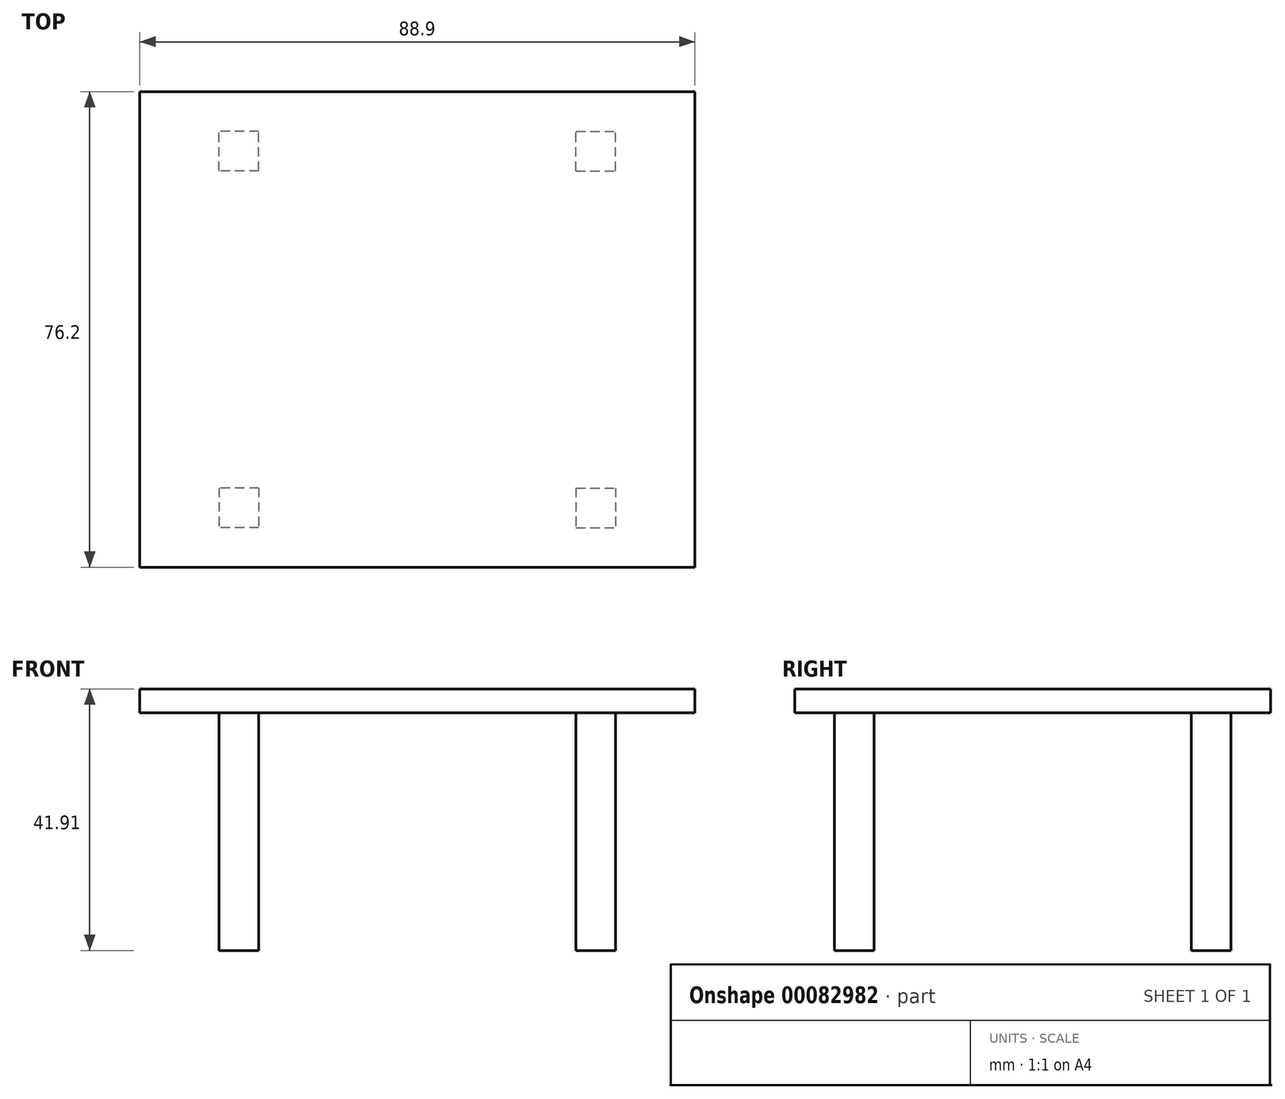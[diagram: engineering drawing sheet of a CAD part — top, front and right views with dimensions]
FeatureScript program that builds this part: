
annotation { "Feature Type Name" : "Feature", "Feature Type Description" : "" }
export const myFeature = defineFeature(function(context is Context, id is Id, definition is map)
    precondition{}
    {
        {
            var Q0;
            Q0=qCreatedBy(makeId("Top.planeOp"),FACE);
            var sketch = newSketch(context, id + "F0", { "sketchPlane" : qUnion([Q0])});
            skLineSegment(sketch, "E0.bottom", {"start": v(-25.4, 25.4) * mm, "end": v(-31.75, 25.4) * mm});
            skLineSegment(sketch, "E0.top", {"start": v(-25.4, 31.75) * mm, "end": v(-31.75, 31.75) * mm});
            skLineSegment(sketch, "E0.left", {"start": v(-25.4, 25.4) * mm, "end": v(-25.4, 31.75) * mm});
            skLineSegment(sketch, "E0.right", {"start": v(-31.75, 25.4) * mm, "end": v(-31.75, 31.75) * mm});
            skSolve(sketch);
        }
        {
            var Q0;
            Q0=makeQuery(id+"F0.imprint","IMPRINT",FACE,{"disambiguationData":[TD([[makeQuery(id+"F0.imprint","IMPRINT",EDGE,{"derivedFrom":sQuery(id+"F0.wireOp",EDGE,"E0.bottom")}),-1.0]])]});
            extrude(context, id + "F1", {"entities" : qUnion([Q0]), "endBound" : BoundingType.SYMMETRIC, "depth" : 38.1 * mm});
        }
        {
            var Q0;
            Q0=makeQuery(id+"F1.opExtrude","SWEPT_BODY",BODY,{"disambiguationData":[OSD([sQuery(id+"F0.wireOp",EDGE,"E0.bottom"),sQuery(id+"F0.wireOp",EDGE,"E0.top"),sQuery(id+"F0.wireOp",EDGE,"E0.left"),sQuery(id+"F0.wireOp",EDGE,"E0.right")])]});
            var Q1;
            Q1=qCreatedBy(makeId("Right.planeOp"),FACE);
            mirror(context, id + "F2", {"entities" : qUnion([Q0]), "mirrorPlane" : qUnion([Q1])});
        }
        {
            var Q0;
            Q0=makeQuery(id+"F1.opExtrude","SWEPT_BODY",BODY,{"disambiguationData":[OSD([sQuery(id+"F0.wireOp",EDGE,"E0.bottom"),sQuery(id+"F0.wireOp",EDGE,"E0.top"),sQuery(id+"F0.wireOp",EDGE,"E0.left"),sQuery(id+"F0.wireOp",EDGE,"E0.right")])]});
            var Q1;
            Q1=makeQuery(id+"F2.opPattern","COPY",BODY,{"derivedFrom":makeQuery(id+"F1.opExtrude","SWEPT_BODY",BODY,{"disambiguationData":[OSD([sQuery(id+"F0.wireOp",EDGE,"E0.bottom"),sQuery(id+"F0.wireOp",EDGE,"E0.top"),sQuery(id+"F0.wireOp",EDGE,"E0.left"),sQuery(id+"F0.wireOp",EDGE,"E0.right")])]}),"instanceName":"1"});
            var Q2;
            Q2=qCreatedBy(makeId("Front.planeOp"),FACE);
            mirror(context, id + "F3", {"entities" : qUnion([Q0, Q1]), "mirrorPlane" : qUnion([Q2])});
        }
        {
            var Q0;
            Q0=makeQuery(id+"F1.opExtrude","CAP_FACE",FACE,{"disambiguationData":[OSD([sQuery(id+"F0.wireOp",EDGE,"E0.bottom"),sQuery(id+"F0.wireOp",EDGE,"E0.top"),sQuery(id+"F0.wireOp",EDGE,"E0.left"),sQuery(id+"F0.wireOp",EDGE,"E0.right")])],"isStart":false});
            var sketch = newSketch(context, id + "F4", { "sketchPlane" : qUnion([Q0])});
            skLineSegment(sketch, "E1.bottom", {"start": v(-44.45, 38.1) * mm, "end": v(44.45, 38.1) * mm});
            skLineSegment(sketch, "E1.top", {"start": v(-44.45, -38.1) * mm, "end": v(44.45, -38.1) * mm});
            skLineSegment(sketch, "E1.left", {"start": v(-44.45, 38.1) * mm, "end": v(-44.45, -38.1) * mm});
            skLineSegment(sketch, "E1.right", {"start": v(44.45, 38.1) * mm, "end": v(44.45, -38.1) * mm});
            skPoint(sketch, "E1.middle", {"position": v(0, 0) * mm});
            skSolve(sketch);
        }
        {
            var Q0;
            Q0=makeQuery(id+"F4.imprint","IMPRINT",FACE,{"disambiguationData":[TD([[makeQuery(id+"F4.imprint","IMPRINT",EDGE,{"derivedFrom":sQuery(id+"F4.wireOp",EDGE,"E1.bottom")}),-1.0]])]});
            var Q1;
            Q1=makeQuery(id+"F4.imprint","IMPRINT",FACE,{"disambiguationData":[TD([[makeQuery(id+"F4.imprint","IMPRINT",EDGE,{"derivedFrom":makeQuery(id+"F1.opExtrude","CAP_EDGE",EDGE,{"disambiguationData":[OSD([sQuery(id+"F0.wireOp",EDGE,"E0.bottom")])],"isStart":false})}),-1.0]])]});
            extrude(context, id + "F5", {"entities" : qUnion([Q0, Q1]), "depth" : 3.8 * mm});
        }
    });
